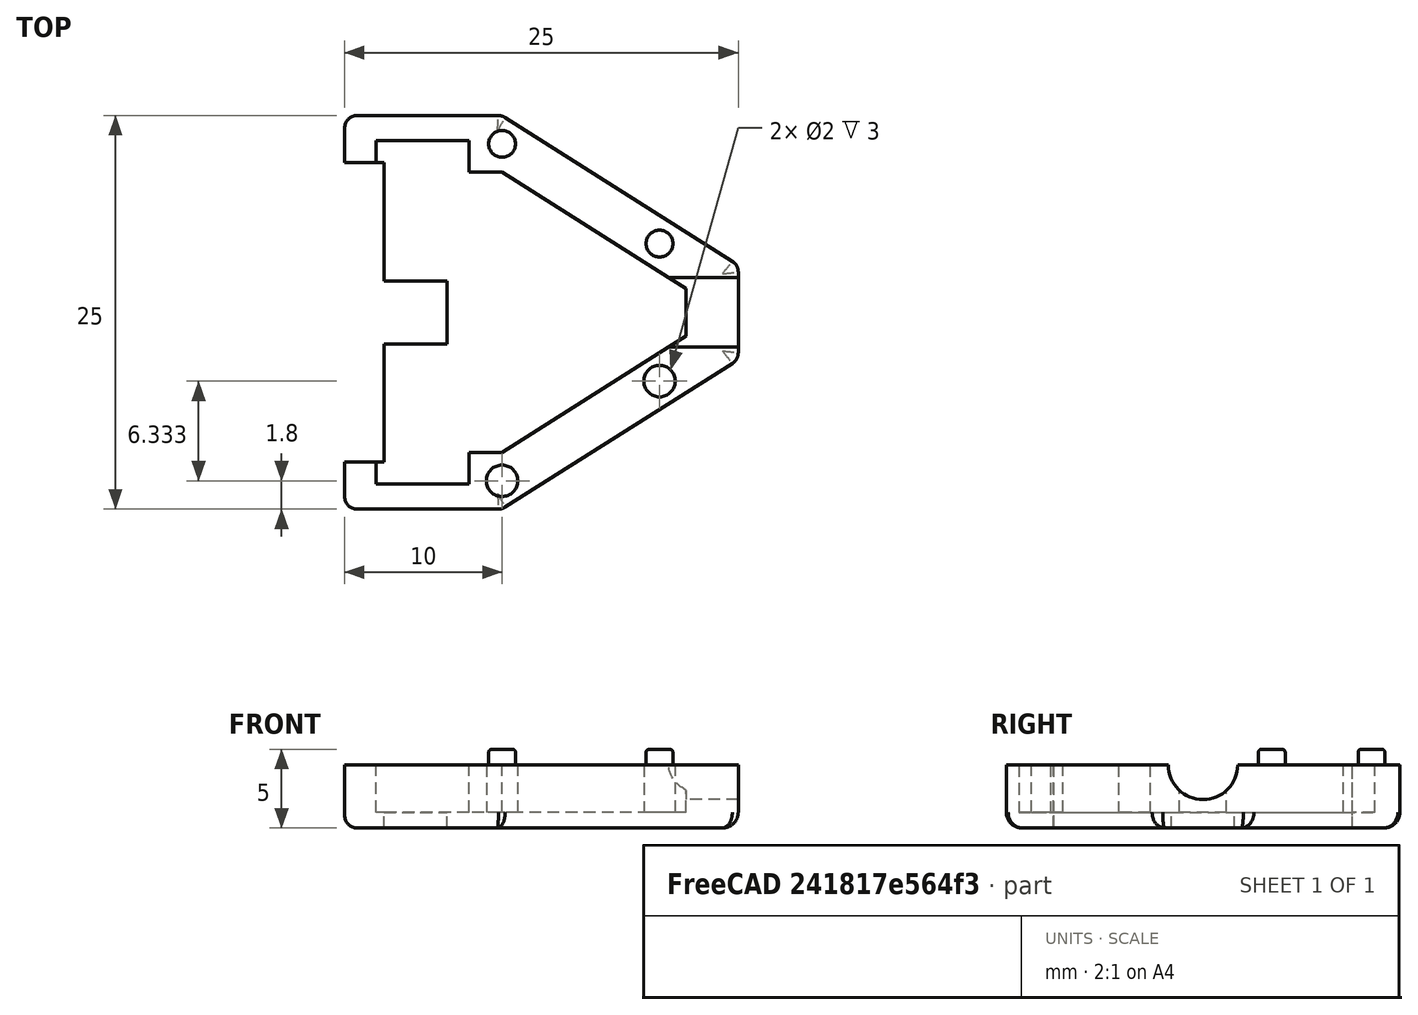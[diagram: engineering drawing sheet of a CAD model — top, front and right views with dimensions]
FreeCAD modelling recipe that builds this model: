
FCSTD DOCUMENT  (FreeCAD 0.21R33694 (Git))
Label: jtag
License: All rights reserved
LicenseURL: http://en.wikipedia.org/wiki/All_rights_reserved
objects: Sketcher::SketchObject×5, PartDesign::Pocket×3, PartDesign::Fillet×3, PartDesign::Pad×2, Spreadsheet::Sheet×1, PartDesign::Body×1, App::Part×1, Mesh::Feature×1
note: 22 computed .brp shape members not serialized (recipe doc carries the construction recipe); baked Part::Feature solids carry a one-line shape summary decoded from their .brp

FEATURE [Sketcher::SketchObject] Sketch  label="Main-Sketch"
  FullyConstrained = true
  MapMode = 5
  Support = -> [XY_Plane001]
  expr: Constraints[11] = <<Parameters>>.shell_length
  expr: Constraints[12] = <<Parameters>>.shell_width_rear
  expr: Constraints[13] = <<Parameters>>.shell_length - 15
  expr: Constraints[7] = Spreadsheet.shell_width_front
  sketch-geometry (6):
    g0: LineSegment StartX=0 StartY=12.5 StartZ=0 EndX=0 EndY=-12.5 EndZ=0
    g1: LineSegment StartX=0 StartY=-12.5 StartZ=0 EndX=10 EndY=-12.5 EndZ=0
    g2: LineSegment StartX=0 StartY=12.5 StartZ=0 EndX=10 EndY=12.5 EndZ=0
    g3: LineSegment StartX=10 StartY=12.5 StartZ=0 EndX=25 EndY=3 EndZ=0
    g4: LineSegment StartX=25 StartY=3 StartZ=0 EndX=25 EndY=-3 EndZ=0
    g5: LineSegment StartX=25 StartY=-3 StartZ=0 EndX=10 EndY=-12.5 EndZ=0
  constraints (16):
    c: Coincident(g1,g0)
    c: Horizontal(g1)
    c: Coincident(g2,g0)
    c: Horizontal(g2)
    c: Coincident(g4,g3)
    c: Coincident(g5,g4)
    c: Symmetric(g0,g0,g-1)
    c: DistanceY(g0,g0) = 25
    c: Symmetric(g4,g3,g-1)
    c: Coincident(g1,g5)
    c: Coincident(g3,g2)
    c: DistanceX(g0,g3) = 25
    c: DistanceY(g4,g3) = 6
    c: DistanceX(g2,g2) = 10
    c: Equal(g2,g1)
    c: PointOnObject(g0,g-2)
FEATURE [Spreadsheet::Sheet] Spreadsheet  label="Parameters"
  cells = A1='Connector; B2='conn_width; C2(conn_width)=21.8; B3='conn_thickness; C3(conn_thickness)=5.6; B4='conn_height; C4(conn_height)=5.9; A7='Backshell; B8='shell_length; C8(shell_length)=25; B9='shell_width_front; C9(shell_width_front)=25; B10='shell_width_rear; C10(shell_width_rear)=6; B11='shell_thickness; C11(shell_thickness)=10; B13='shell_wall; C13(shell_wall)=2
FEATURE [PartDesign::Pad] Pad  label="Main-Pad"
  Direction = (0,0,1)
  Length = 4
  Length2 = 10
  Profile = -> Sketch
  ReferenceAxis = -> Sketch [N_Axis]
  Type = 0
  expr: Length = <<Parameters>>.conn_thickness / 2 + <<Parameters>>.shell_wall / 2 + 0.2
FEATURE [Sketcher::SketchObject] Sketch001  label="Inside-Sketch"
  AttachmentOffset = pos=(0,0,1) rot=(0,0,1;0rad)
  ExternalGeometry = -> [Sketch]
  FullyConstrained = true
  MapMode = 5
  Placement = pos=(0,0,1) rot=(0,0,1;0rad)
  Support = -> [XY_Plane001]
  expr: .AttachmentOffset.Base.z = Spreadsheet.shell_wall / 2
  expr: Constraints[13] = <<Parameters>>.shell_length - 15
  expr: Constraints[31] = Spreadsheet.conn_width
  expr: Constraints[36] = <<Parameters>>.conn_height
  sketch-geometry (17):
    g0: LineSegment StartX=7.9 StartY=-8.9 StartZ=0 EndX=10 EndY=-8.9 EndZ=0
    g1: LineSegment StartX=10 StartY=-8.9 StartZ=0 EndX=21.6842 EndY=-1.5 EndZ=0
    g2: LineSegment StartX=21.6842 StartY=1.5 StartZ=0 EndX=10 EndY=8.9 EndZ=0
    g3: LineSegment StartX=10 StartY=8.9 StartZ=0 EndX=7.9 EndY=8.9 EndZ=0
    g4: LineSegment StartX=7.9 StartY=8.9 StartZ=0 EndX=7.9 EndY=10.9 EndZ=0
    g5: LineSegment StartX=7.9 StartY=-8.9 StartZ=0 EndX=7.9 EndY=-10.9 EndZ=0
    g6: LineSegment StartX=21.6842 StartY=1.5 StartZ=0 EndX=21.6842 EndY=-1.5 EndZ=0
    g7: LineSegment StartX=7.9 StartY=10.9 StartZ=0 EndX=2 EndY=10.9 EndZ=0
    g8: LineSegment StartX=2 StartY=10.9 StartZ=0 EndX=2 EndY=8.9 EndZ=0
    g9: LineSegment StartX=2 StartY=8.9 StartZ=0 EndX=0 EndY=8.9 EndZ=0
    g10: LineSegment StartX=7.9 StartY=-10.9 StartZ=0 EndX=2 EndY=-10.9 EndZ=0
    g11: LineSegment StartX=2 StartY=-10.9 StartZ=0 EndX=2 EndY=-8.9 EndZ=0
    g12: LineSegment StartX=2 StartY=-8.9 StartZ=0 EndX=0 EndY=-8.9 EndZ=0
    g13: LineSegment StartX=0 StartY=8.9 StartZ=0 EndX=0 EndY=-8.9 EndZ=0
    g14: Circle CenterX=10 CenterY=-10.7 CenterZ=0 NormalX=0 NormalY=0 NormalZ=1 AngleXU=0 Radius=1
    g15: Circle CenterX=20 CenterY=-4.36667 CenterZ=0 NormalX=0 NormalY=0 NormalZ=1 AngleXU=0 Radius=1
    g16: LineSegment StartX=10 StartY=-10.7 StartZ=0 EndX=20 EndY=-4.36667 EndZ=0
  constraints (47):
    c: Horizontal(g0)
    c: Horizontal(g3)
    c: Symmetric(g3,g0,g-1)
    c: Equal(g3,g0)
    c: Coincident(g3,g2)
    c: Coincident(g0,g1)
    c: Coincident(g4,g3)
    c: Vertical(g4)
    c: PointOnObject(g9,g-2)
    c: Coincident(g5,g0)
    c: Vertical(g5)
    c: PointOnObject(g12,g-2)
    c: DistanceY(g4,g4) = 2
    c: DistanceX(g9,g2) = 10
    c: Parallel(g2,g-4)
    c: Coincident(g6,g2)
    c: Coincident(g6,g1)
    c: Symmetric(g2,g1,g-1)
    c: DistanceY(g6,g6) = 3
    c: Coincident(g4,g7)
    c: Horizontal(g7)
    c: Coincident(g7,g8)
    c: Vertical(g8)
    c: Coincident(g8,g9)
    c: Horizontal(g9)
    c: Coincident(g5,g10)
    c: Horizontal(g10)
    c: Coincident(g10,g11)
    c: Vertical(g11)
    c: Coincident(g11,g12)
    c: Horizontal(g12)
    c: DistanceY(g10,g7) = 21.8
    c: Equal(g8,g4)
    c: Equal(g4,g5)
    c: Equal(g5,g11)
    c: Equal(g12,g9)
    c: DistanceX(g10,g5) = 5.9
    c: DistanceX(g9,g8) = 2
    c: Coincident(g13,g12)
    c: Coincident(g13,g9)
    c: Equal(g14,g15)
    c: Radius(g15) = 1
    c: Symmetric(g0,g-3,g14)
    c: DistanceX(g14,g15) = 10
    c: Coincident(g16,g14)
    c: Coincident(g16,g15)
    c: Parallel(g16,g1)
FEATURE [PartDesign::Pocket] Pocket  label="Inside-Pocket"
  BaseFeature = -> Pad
  Direction = (0,0,-1)
  Length = 5
  Length2 = 5
  Profile = -> Sketch001
  ReferenceAxis = -> Sketch001 [N_Axis]
  Reversed = true
  Type = 0
FEATURE [Sketcher::SketchObject] Sketch002  label="Hole-Sketch"
  FullyConstrained = true
  MapMode = 5
  Placement = pos=(0,0,0) rot=(0.57735,0.57735,0.57735;2.0944rad)
  Support = -> [YZ_Plane001]
  expr: Constraints[1] = Spreadsheet.conn_thickness / 2 + 1.2
  sketch-geometry (1):
    g0: Circle CenterX=0 CenterY=4 CenterZ=0 NormalX=0 NormalY=0 NormalZ=1 AngleXU=0 Radius=2.2
  constraints (3):
    c: PointOnObject(g0,g-2)
    c: DistanceY(g-1,g0) = 4
    c: Radius(g0) = 2.2
FEATURE [PartDesign::Pocket] Pocket001  label="Hole-Pocket"
  BaseFeature = -> Pocket
  Direction = (-1,2e-16,-3e-16)
  Length = 5
  Length2 = 5
  Profile = -> Sketch002
  ReferenceAxis = -> Sketch002 [N_Axis]
  Reversed = true
  Type = 1
FEATURE [Sketcher::SketchObject] Sketch003  label="Key-Sketch"
  FullyConstrained = true
  MapMode = 5
  Support = -> [XY_Plane001]
  expr: Constraints[6] = <<Parameters>>.shell_width_front - 6
  sketch-geometry (8):
    g0: LineSegment StartX=-2.5 StartY=9.5 StartZ=0 EndX=2.5 EndY=9.5 EndZ=0
    g1: LineSegment StartX=2.5 StartY=-9.5 StartZ=0 EndX=-2.5 EndY=-9.5 EndZ=0
    g2: LineSegment StartX=-2.5 StartY=-9.5 StartZ=0 EndX=-2.5 EndY=9.5 EndZ=0
    g3: LineSegment StartX=2.5 StartY=9.5 StartZ=0 EndX=2.5 EndY=2 EndZ=0
    g4: LineSegment StartX=2.5 StartY=2 StartZ=0 EndX=6.5 EndY=2 EndZ=0
    g5: LineSegment StartX=6.5 StartY=2 StartZ=0 EndX=6.5 EndY=-2 EndZ=0
    g6: LineSegment StartX=6.5 StartY=-2 StartZ=0 EndX=2.5 EndY=-2 EndZ=0
    g7: LineSegment StartX=2.5 StartY=-2 StartZ=0 EndX=2.5 EndY=-9.5 EndZ=0
  constraints (22):
    c: Coincident(g1,g2)
    c: Coincident(g2,g0)
    c: Horizontal(g0)
    c: Horizontal(g1)
    c: Vertical(g2)
    c: Symmetric(g0,g1,g-1)
    c: DistanceY(g1,g0) = 19
    c: DistanceX(g0,g0) = 5
    c: Coincident(g0,g3)
    c: Vertical(g3)
    c: Coincident(g3,g4)
    c: Horizontal(g4)
    c: Coincident(g4,g5)
    c: Vertical(g5)
    c: Coincident(g5,g6)
    c: Horizontal(g6)
    c: Coincident(g6,g7)
    c: Coincident(g7,g1)
    c: Vertical(g7)
    c: Symmetric(g3,g6,g-1)
    c: DistanceY(g5,g5) = 4
    c: DistanceX(g4,g4) = 4
FEATURE [PartDesign::Pocket] Pocket002  label="Key-Pocket"
  BaseFeature = -> Pocket001
  Direction = (0,0,-1)
  Length = 5
  Length2 = 5
  Profile = -> Sketch003
  ReferenceAxis = -> Sketch003 [N_Axis]
  Reversed = true
  Type = 0
FEATURE [Sketcher::SketchObject] Sketch004  label="Pins-Sketch"
  AttachmentOffset = pos=(0,0,1) rot=(0,0,1;0rad)
  ExternalGeometry = -> [Sketch001,Sketch]
  FullyConstrained = true
  MapMode = 5
  Placement = pos=(0,0,1) rot=(0,0,1;0rad)
  Support = -> [XY_Plane001]
  sketch-geometry (3):
    g0: Circle CenterX=10 CenterY=10.7 CenterZ=0 NormalX=0 NormalY=0 NormalZ=1 AngleXU=0 Radius=0.85
    g1: Circle CenterX=20 CenterY=4.36667 CenterZ=0 NormalX=0 NormalY=0 NormalZ=1 AngleXU=0 Radius=0.85
    g2: LineSegment StartX=10 StartY=10.7 StartZ=0 EndX=20 EndY=4.36667 EndZ=0
  constraints (7):
    c: Equal(g0,g1)
    c: Radius(g1) = 0.85
    c: DistanceX(g0,g1) = 10
    c: Symmetric(g-6,g-5,g0)
    c: Coincident(g2,g0)
    c: Coincident(g2,g1)
    c: Parallel(g-5,g2)
FEATURE [PartDesign::Pad] Pad001  label="Pins-Pad"
  BaseFeature = -> Pocket002
  Direction = (0,0,1)
  Length = 4
  Length2 = 10
  Profile = -> Sketch004
  ReferenceAxis = -> Sketch004 [N_Axis]
  Type = 0
  expr: Length = <<Parameters>>.shell_thickness / 2 - 1
FEATURE [PartDesign::Fillet] Fillet
  Base = -> Pad001 [Edge80,Edge78]
  BaseFeature = -> Pad001
  Radius = 0.2
  SupportTransform = false
  UseAllEdges = false
FEATURE [PartDesign::Fillet] Fillet001
  Base = -> Fillet [Edge49,Edge24,Edge50,Edge20,Edge29]
  BaseFeature = -> Fillet
  Radius = 1
  SupportTransform = false
  UseAllEdges = false
FEATURE [PartDesign::Fillet] Fillet002
  Base = -> Fillet001 [Edge64,Edge1,Edge90,Edge40,Edge23,Edge4]
  BaseFeature = -> Fillet001
  Radius = 0.8
  SupportTransform = false
  UseAllEdges = false
FEATURE [PartDesign::Body] Body
  Group = -> [Sketch,Pad,Sketch001,Pocket,Sketch002,Pocket001,Sketch003,Pocket002,Sketch004,Pad001,Fillet,Fillet001,Fillet002]
  Origin = -> Origin001
  Tip = -> Fillet002
FEATURE [App::Part] Part
  Group = -> [Body]
  Origin = -> Origin
FEATURE [Mesh::Feature] Mesh  label="Fillet002 (Meshed)"
